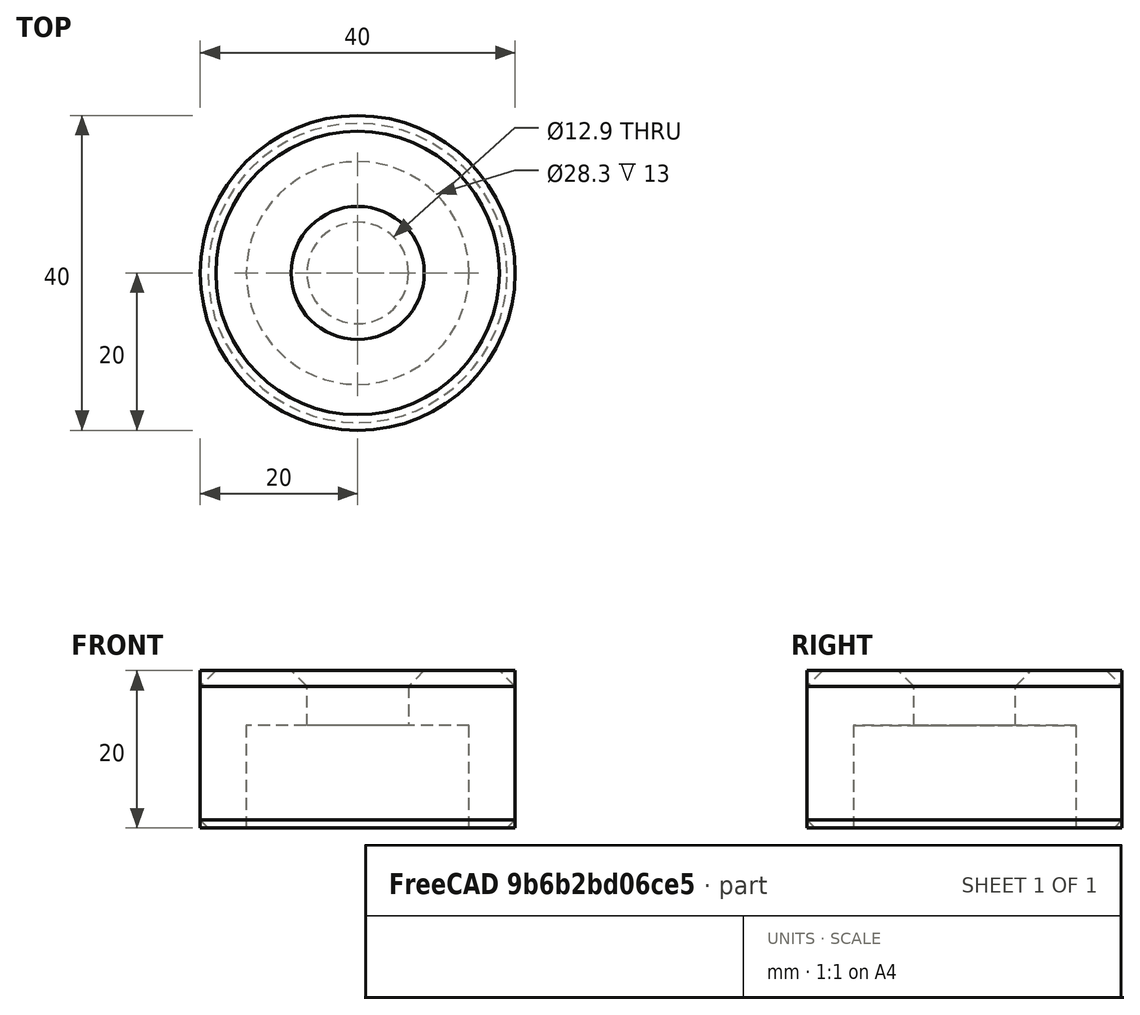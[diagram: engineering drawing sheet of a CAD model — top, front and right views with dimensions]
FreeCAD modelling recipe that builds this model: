
FCSTD DOCUMENT  (FreeCAD 0.16R)
Label: PressBushing
License: All rights reserved
LicenseURL: http://en.wikipedia.org/wiki/All_rights_reserved
objects: Sketcher::SketchObject×3, PartDesign::Chamfer×3, PartDesign::Pocket×2, PartDesign::Pad×1, Mesh::Feature×1
note: 12 computed .brp shape members not serialized (recipe doc carries the construction recipe); baked Part::Feature solids carry a one-line shape summary decoded from their .brp

FEATURE [Sketcher::SketchObject] Sketch
  sketch-geometry (1):
    g0: Circle CenterX=0 CenterY=0 CenterZ=0 NormalX=0 NormalY=0 NormalZ=1 Radius=20
  constraints (2):
    c: Radius(g0) = 20
    c: Coincident(g0,g-1)
FEATURE [PartDesign::Pad] Pad
  Length = 20
  Length2 = 100
  Sketch = -> Sketch
  Type = 0
FEATURE [Sketcher::SketchObject] Sketch001
  Placement = pos=(0,0,0) rot=(1,0,0;3.14159rad)
  Support = -> Pad [Face2]
  sketch-geometry (1):
    g0: Circle CenterX=0 CenterY=0 CenterZ=0 NormalX=0 NormalY=0 NormalZ=1 Radius=14.15
  constraints (2):
    c: Radius(g0) = 14.15
    c: Coincident(g0,g-1)
FEATURE [PartDesign::Pocket] Pocket
  Length = 13
  Sketch = -> Sketch001
  Type = 0
FEATURE [Sketcher::SketchObject] Sketch002
  Placement = pos=(0,0,20) rot=(0,0,1;0rad)
  Support = -> Pocket [Face3]
  sketch-geometry (1):
    g0: Circle CenterX=0 CenterY=0 CenterZ=0 NormalX=0 NormalY=0 NormalZ=1 Radius=6.45
  constraints (2):
    c: Radius(g0) = 6.45
    c: Coincident(g0,g-1)
FEATURE [PartDesign::Pocket] Pocket001
  Length = 5
  Sketch = -> Sketch002
  Type = 1
FEATURE [PartDesign::Chamfer] Chamfer
  Base = -> Pocket001 [Edge3]
  Size = 2
FEATURE [PartDesign::Chamfer] Chamfer001
  Base = -> Chamfer [Edge3]
  Size = 1
FEATURE [PartDesign::Chamfer] Chamfer002
  Base = -> Chamfer001 [Edge9]
  Size = 2
FEATURE [Mesh::Feature] Mesh  label="Chamfer002 (Meshed)"
